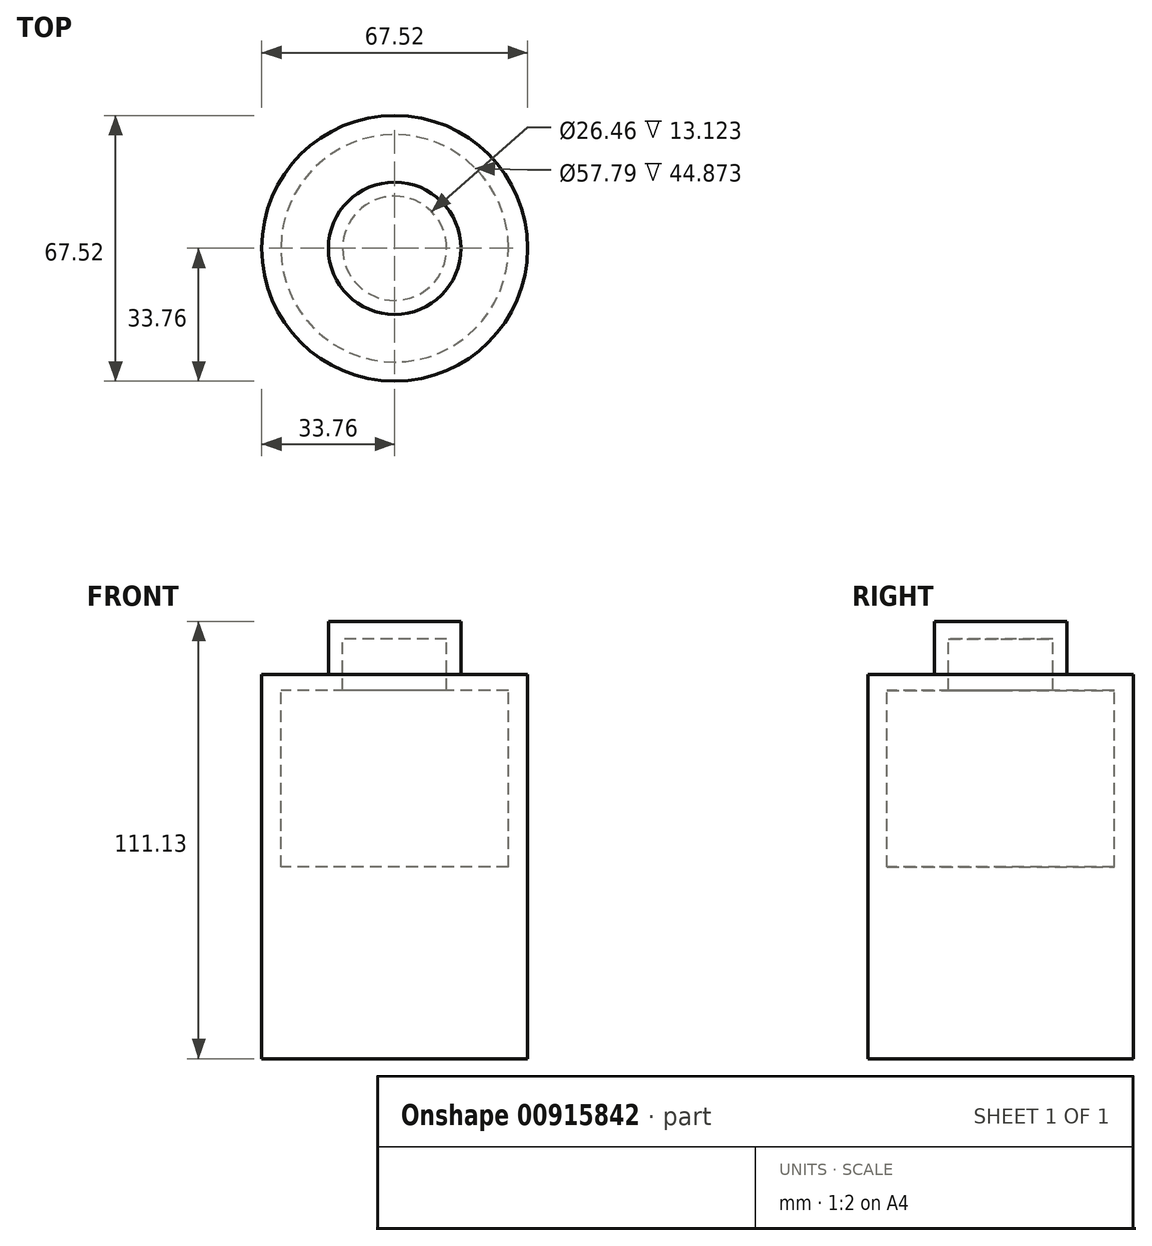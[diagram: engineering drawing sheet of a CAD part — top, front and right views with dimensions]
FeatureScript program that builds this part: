
annotation { "Feature Type Name" : "Feature", "Feature Type Description" : "" }
export const myFeature = defineFeature(function(context is Context, id is Id, definition is map)
    precondition{}
    {
        {
            var Q0;
            Q0=qCreatedBy(makeId("Front.planeOp"),FACE);
            var sketch = newSketch(context, id + "F0", { "sketchPlane" : qUnion([Q0])});
            skLineSegment(sketch, "E0", {"start": v(0, 61.07) * mm, "end": v(0, -57.26) * mm, "construction": true});
            skLineSegment(sketch, "E1", {"start": v(0, 55.99) * mm, "end": v(16.83, 55.99) * mm});
            skLineSegment(sketch, "E2", {"start": v(16.83, 55.99) * mm, "end": v(16.83, 42.44) * mm});
            skLineSegment(sketch, "E3", {"start": v(16.83, 42.44) * mm, "end": v(33.76, 42.44) * mm});
            skLineSegment(sketch, "E4", {"start": v(33.76, 42.44) * mm, "end": v(33.76, -55.14) * mm});
            skLineSegment(sketch, "E5", {"start": v(33.76, -55.14) * mm, "end": v(0, -55.14) * mm});
            skLineSegment(sketch, "E6", {"start": v(0, -55.14) * mm, "end": v(0, -6.46) * mm});
            skLineSegment(sketch, "E7", {"start": v(0, -6.46) * mm, "end": v(28.9, -6.46) * mm});
            skLineSegment(sketch, "E8", {"start": v(28.9, -6.46) * mm, "end": v(28.9, 36.3) * mm});
            skLineSegment(sketch, "E9", {"start": v(28.9, 36.3) * mm, "end": v(28.9, 38.42) * mm});
            skLineSegment(sketch, "E10", {"start": v(28.9, 38.42) * mm, "end": v(13.23, 38.42) * mm});
            skLineSegment(sketch, "E11", {"start": v(13.23, 38.42) * mm, "end": v(13.23, 51.54) * mm});
            skLineSegment(sketch, "E12", {"start": v(13.23, 51.54) * mm, "end": v(0, 51.54) * mm});
            skLineSegment(sketch, "E13", {"start": v(0, 51.54) * mm, "end": v(0, 55.99) * mm});
            skSolve(sketch);
        }
        {
            var Q0;
            Q0=makeQuery(id+"F0.imprint","IMPRINT",FACE,{"disambiguationData":[TD([[makeQuery(id+"F0.imprint","IMPRINT",EDGE,{"derivedFrom":sQuery(id+"F0.wireOp",EDGE,"E1")}),-1.0]])]});
            var Q1;
            Q1=sQuery(id+"F0.wireOp",EDGE,"E4");
            var Q2;
            Q2=sQuery(id+"F0.wireOp",EDGE,"E2");
            var Q3;
            Q3=sQuery(id+"F0.wireOp",EDGE,"E1");
            var Q4;
            Q4=sQuery(id+"F0.wireOp",EDGE,"E3");
            var Q5;
            Q5=sQuery(id+"F0.wireOp",EDGE,"E5");
            var Q6;
            Q6=sQuery(id+"F0.wireOp",EDGE,"E0");
            revolve(context, id + "F1", {"surfaceOperationType" : NewSurfaceOperationType.NEW, "entities" : qUnion([Q0]), "surfaceEntities" : qUnion([Q1, Q2, Q3, Q4, Q5]), "axis" : qUnion([Q6]), "revolveType" : RevolveType.FULL});
        }
    });
